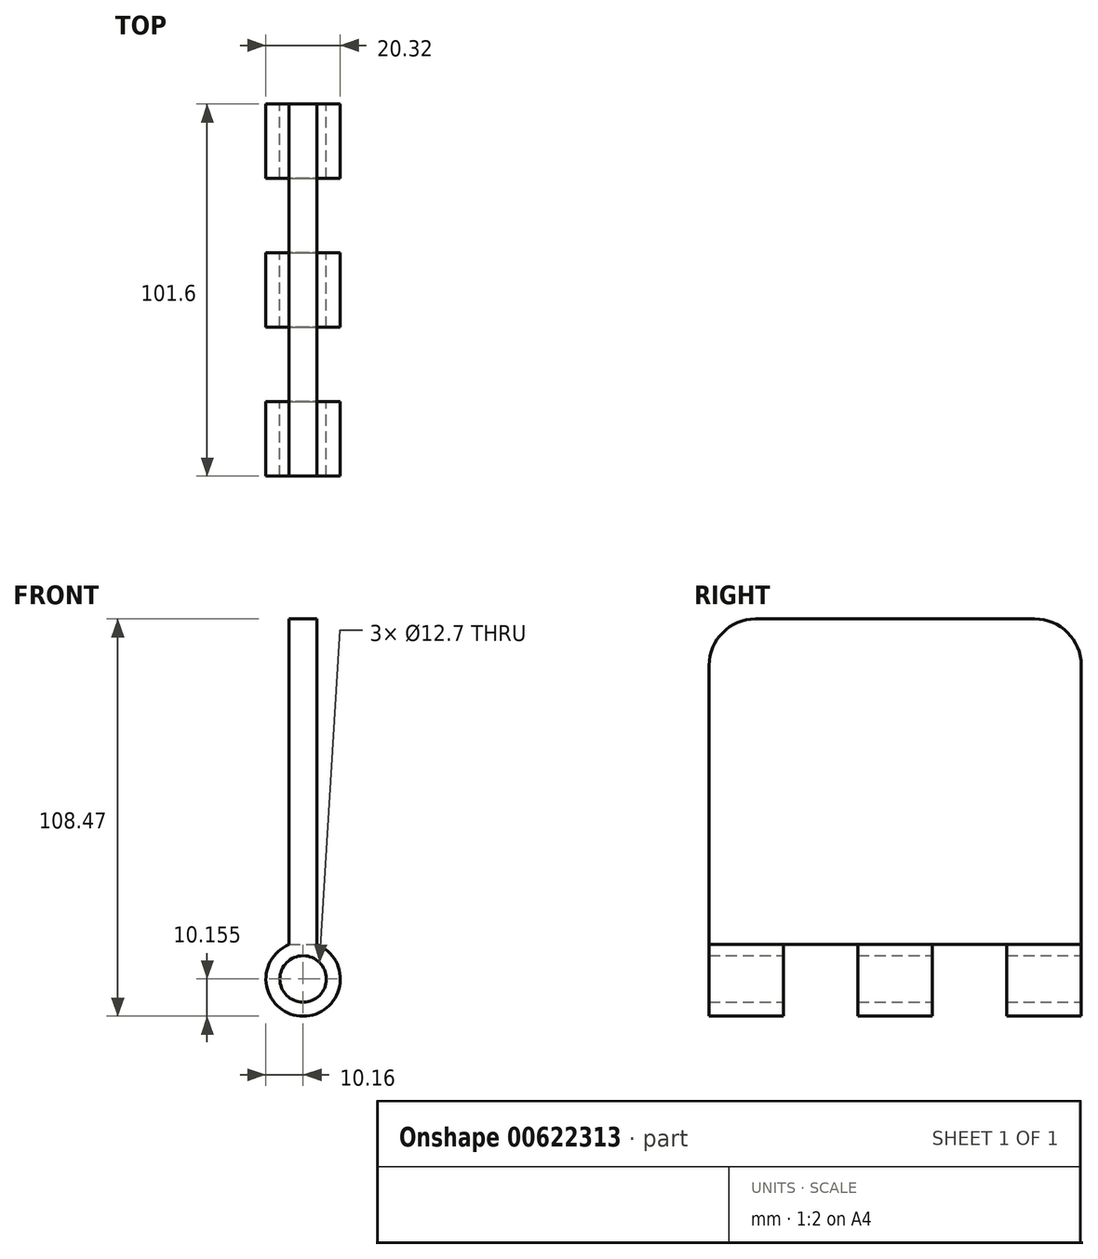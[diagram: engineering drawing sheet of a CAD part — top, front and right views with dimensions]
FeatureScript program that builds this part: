
annotation { "Feature Type Name" : "Feature", "Feature Type Description" : "" }
export const myFeature = defineFeature(function(context is Context, id is Id, definition is map)
    precondition{}
    {
        {
            var Q0;
            Q0=qCreatedBy(makeId("Front.planeOp"),FACE);
            var sketch = newSketch(context, id + "F0", { "sketchPlane" : qUnion([Q0])});
            skLineSegment(sketch, "E0", {"start": v(-3.81, 51.17) * mm, "end": v(3.81, 51.17) * mm});
            skLineSegment(sketch, "E1", {"start": v(3.8, 51.17) * mm, "end": v(3.81, -37.73) * mm});
            skArc(sketch, "E2", {"start": v(-3.8, -37.73) * mm, "mid": v(0, -57.3) * mm, "end": v(3.81, -37.73) * mm});
            skLineSegment(sketch, "E3", {"start": v(-3.81, 51.17) * mm, "end": v(-3.8, -37.73) * mm});
            skLineSegment(sketch, "E4", {"start": v(0, 67.6) * mm, "end": v(0, -41.82) * mm, "construction": true});
            skSolve(sketch);
        }
        {
            var Q0;
            Q0 = qSketchRegion(id + "F0", true);
            extrude(context, id + "F1", {"entities" : qUnion([Q0]), "depth" : 101.6 * mm, "offsetDistance" : 25.4 * mm});
        }
        {
            var Q0;
            Q0=makeQuery(id+"F1.opExtrude","CAP_EDGE",EDGE,{"disambiguationData":[OSD([sQuery(id+"F0.wireOp",EDGE,"E0")])],"isStart":false});
            var Q1;
            Q1=makeQuery(id+"F1.opExtrude","CAP_EDGE",EDGE,{"disambiguationData":[OSD([sQuery(id+"F0.wireOp",EDGE,"E0")])],"isStart":true});
            fillet(context, id + "F2", {"entities" : qUnion([Q0, Q1]), "radius" : 12.7 * mm, "tangentPropagation" : true, "allowEdgeOverflow" : false});
        }
        {
            var Q0;
            Q0=makeQuery(id+"F1.opExtrude","CAP_FACE",FACE,{"disambiguationData":[OSD([sQuery(id+"F0.wireOp",EDGE,"E0"),sQuery(id+"F0.wireOp",EDGE,"E1"),sQuery(id+"F0.wireOp",EDGE,"E2"),sQuery(id+"F0.wireOp",EDGE,"E3")])],"isStart":true});
            var sketch = newSketch(context, id + "F3", { "sketchPlane" : qUnion([Q0])});
            skCircle(sketch, "E5", {"center": v(0, -47.14) * mm, "radius": 6.35 * mm});
            skSolve(sketch);
        }
        {
            var Q0;
            Q0=makeQuery(id+"F3.imprint","IMPRINT",FACE,{"disambiguationData":[TD([[makeQuery(id+"F3.imprint","IMPRINT",EDGE,{"derivedFrom":sQuery(id+"F3.wireOp",EDGE,"E5")}),1.0]])]});
            extrude(context, id + "F4", {"entities" : qUnion([Q0]), "operationType" : NewBodyOperationType.REMOVE, "endBound" : BoundingType.THROUGH_ALL, "oppositeDirection" : true, "depth" : 25.4 * mm, "offsetDistance" : 25.4 * mm});
        }
        {
            var Q0;
            Q0=makeQuery(id+"F1.opExtrude","SWEPT_FACE",FACE,{"disambiguationData":[OSD([sQuery(id+"F0.wireOp",EDGE,"E1")])]});
            var sketch = newSketch(context, id + "F5", { "sketchPlane" : qUnion([Q0])});
            skLineSegment(sketch, "E6.bottom", {"start": v(-81.28, -62.09) * mm, "end": v(-60.96, -62.09) * mm});
            skLineSegment(sketch, "E6.top", {"start": v(-81.28, -37.73) * mm, "end": v(-60.96, -37.73) * mm});
            skLineSegment(sketch, "E6.left", {"start": v(-81.28, -62.09) * mm, "end": v(-81.28, -37.73) * mm});
            skLineSegment(sketch, "E6.right", {"start": v(-60.96, -62.09) * mm, "end": v(-60.96, -37.73) * mm});
            skLineSegment(sketch, "E7.bottom", {"start": v(-40.64, -61.48) * mm, "end": v(-20.32, -61.48) * mm});
            skLineSegment(sketch, "E7.top", {"start": v(-40.64, -37.73) * mm, "end": v(-20.32, -37.73) * mm});
            skLineSegment(sketch, "E7.left", {"start": v(-40.64, -61.48) * mm, "end": v(-40.64, -37.73) * mm});
            skLineSegment(sketch, "E7.right", {"start": v(-20.32, -61.48) * mm, "end": v(-20.32, -37.73) * mm});
            skSolve(sketch);
        }
        {
            var Q0;
            Q0=makeQuery(id+"F5.imprint","IMPRINT",FACE,{"disambiguationData":[TD([[makeQuery(id+"F5.imprint","IMPRINT",EDGE,{"derivedFrom":sQuery(id+"F5.wireOp",EDGE,"E6.bottom")}),1.0]])]});
            var Q1;
            Q1=makeQuery(id+"F5.imprint","IMPRINT",FACE,{"disambiguationData":[TD([[makeQuery(id+"F5.imprint","IMPRINT",EDGE,{"derivedFrom":sQuery(id+"F5.wireOp",EDGE,"E7.bottom")}),1.0]])]});
            extrude(context, id + "F6", {"entities" : qUnion([Q0, Q1]), "operationType" : NewBodyOperationType.REMOVE, "oppositeDirection" : true, "depth" : 101.6 * mm, "offsetDistance" : 25.4 * mm, "symmetric" : true});
        }
    });
